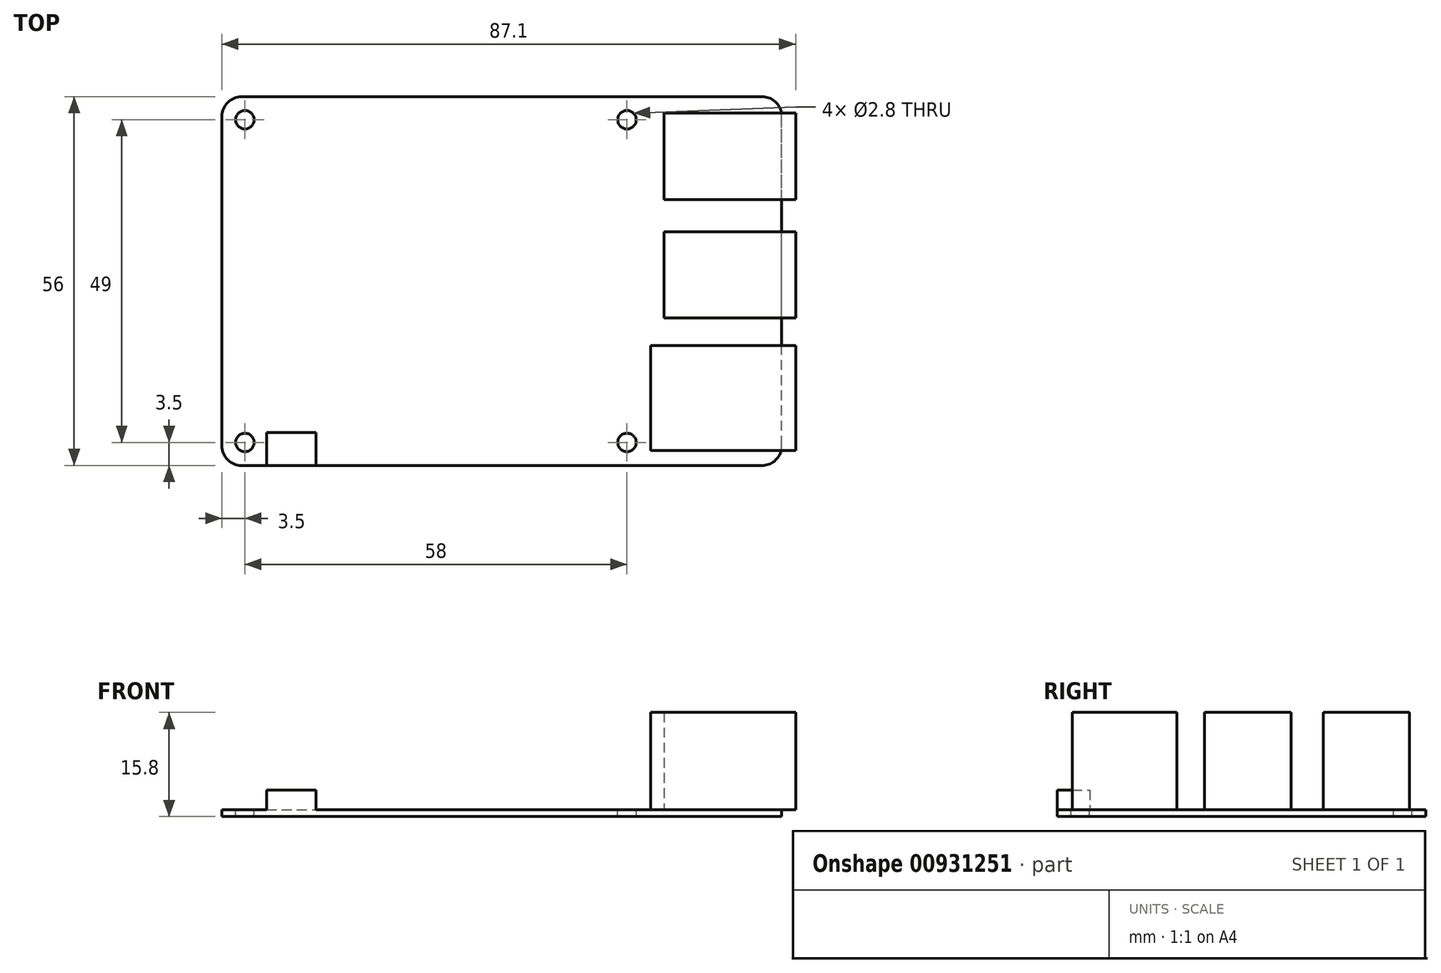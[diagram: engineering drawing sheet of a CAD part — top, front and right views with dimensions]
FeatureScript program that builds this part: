
annotation { "Feature Type Name" : "Feature", "Feature Type Description" : "" }
export const myFeature = defineFeature(function(context is Context, id is Id, definition is map)
    precondition{}
    {
        {
            var Q0;
            Q0=qCreatedBy(makeId("Top.planeOp"),FACE);
            var sketch = newSketch(context, id + "F0", { "sketchPlane" : qUnion([Q0])});
            skLineSegment(sketch, "E0.bottom", {"start": v(-42.5, -28) * mm, "end": v(42.5, -28) * mm});
            skLineSegment(sketch, "E0.top", {"start": v(-42.5, 28) * mm, "end": v(42.5, 28) * mm});
            skLineSegment(sketch, "E0.left", {"start": v(-42.5, -28) * mm, "end": v(-42.5, 28) * mm});
            skLineSegment(sketch, "E0.right", {"start": v(42.5, -28) * mm, "end": v(42.5, 28) * mm});
            skSolve(sketch);
        }
        {
            var Q0;
            Q0=qSketchRegion(id+"F0",true);
            extrude(context, id + "F1", {"entities" : qUnion([Q0]), "depth" : 1 * mm, "offsetDistance" : 25 * mm});
        }
        {
            var Q0;
            Q0=makeQuery(id+"F1.opExtrude","SWEPT_EDGE",EDGE,{"disambiguationData":[OSD([sQuery(id+"F0.wireOp",EDGE,"E0.bottom"),sQuery(id+"F0.wireOp",EDGE,"E0.right")])]});
            var Q1;
            Q1=makeQuery(id+"F1.opExtrude","SWEPT_EDGE",EDGE,{"disambiguationData":[OSD([sQuery(id+"F0.wireOp",EDGE,"E0.top"),sQuery(id+"F0.wireOp",EDGE,"E0.right")])]});
            var Q2;
            Q2=makeQuery(id+"F1.opExtrude","SWEPT_EDGE",EDGE,{"disambiguationData":[OSD([sQuery(id+"F0.wireOp",EDGE,"E0.top"),sQuery(id+"F0.wireOp",EDGE,"E0.left")])]});
            var Q3;
            Q3=makeQuery(id+"F1.opExtrude","SWEPT_EDGE",EDGE,{"disambiguationData":[OSD([sQuery(id+"F0.wireOp",EDGE,"E0.bottom"),sQuery(id+"F0.wireOp",EDGE,"E0.left")])]});
            fillet(context, id + "F2", {"entities" : qUnion([Q0, Q1, Q2, Q3]), "radius" : 3 * mm, "tangentPropagation" : true, "allowEdgeOverflow" : false});
        }
        {
            var Q0;
            Q0=makeQuery(id+"F1.opExtrude","CAP_FACE",FACE,{"disambiguationData":[OSD([sQuery(id+"F0.wireOp",EDGE,"E0.bottom"),sQuery(id+"F0.wireOp",EDGE,"E0.top"),sQuery(id+"F0.wireOp",EDGE,"E0.left"),sQuery(id+"F0.wireOp",EDGE,"E0.right")])],"isStart":false});
            var sketch = newSketch(context, id + "F3", { "sketchPlane" : qUnion([Q0])});
            skLineSegment(sketch, "E1.bottom", {"start": v(44.6, -25.7) * mm, "end": v(22.6, -25.7) * mm});
            skLineSegment(sketch, "E1.top", {"start": v(44.6, -9.8) * mm, "end": v(22.6, -9.8) * mm});
            skLineSegment(sketch, "E1.left", {"start": v(44.6, -25.7) * mm, "end": v(44.6, -9.8) * mm});
            skLineSegment(sketch, "E1.right", {"start": v(22.6, -25.7) * mm, "end": v(22.6, -9.8) * mm});
            skLineSegment(sketch, "E2.bottom", {"start": v(24.6, 7.5) * mm, "end": v(44.6, 7.5) * mm});
            skLineSegment(sketch, "E2.top", {"start": v(24.6, -5.6) * mm, "end": v(44.6, -5.6) * mm});
            skLineSegment(sketch, "E2.left", {"start": v(24.6, 7.5) * mm, "end": v(24.6, -5.6) * mm});
            skLineSegment(sketch, "E2.right", {"start": v(44.6, 7.5) * mm, "end": v(44.6, -5.6) * mm});
            skLineSegment(sketch, "E3.bottom", {"start": v(24.6, 25.5) * mm, "end": v(44.6, 25.5) * mm});
            skLineSegment(sketch, "E3.top", {"start": v(24.6, 12.4) * mm, "end": v(44.6, 12.4) * mm});
            skLineSegment(sketch, "E3.left", {"start": v(24.6, 25.5) * mm, "end": v(24.6, 12.4) * mm});
            skLineSegment(sketch, "E3.right", {"start": v(44.6, 25.5) * mm, "end": v(44.6, 12.4) * mm});
            skSolve(sketch);
        }
        {
            var Q0;
            Q0=qSketchRegion(id+"F3",true);
            extrude(context, id + "F4", {"entities" : qUnion([Q0]), "operationType" : NewBodyOperationType.ADD, "depth" : 14.8 * mm, "offsetDistance" : 25 * mm});
        }
        {
            var Q0;
            Q0=makeQuery(id+"F1.opExtrude","CAP_FACE",FACE,{"disambiguationData":[OSD([sQuery(id+"F0.wireOp",EDGE,"E0.bottom"),sQuery(id+"F0.wireOp",EDGE,"E0.top"),sQuery(id+"F0.wireOp",EDGE,"E0.left"),sQuery(id+"F0.wireOp",EDGE,"E0.right")])],"isStart":false});
            var sketch = newSketch(context, id + "F5", { "sketchPlane" : qUnion([Q0])});
            skPoint(sketch, "E4", {"position": v(-39, 24.5) * mm});
            skPoint(sketch, "E5", {"position": v(-39, -24.5) * mm});
            skPoint(sketch, "E6", {"position": v(19, -24.5) * mm});
            skPoint(sketch, "E7", {"position": v(19, 24.5) * mm});
            skSolve(sketch);
        }
        {
            var Q0;
            Q0=sQuery(id+"F5.wireOp",VERTEX,"E4");
            var Q1;
            Q1=sQuery(id+"F5.wireOp",VERTEX,"E7");
            var Q2;
            Q2=sQuery(id+"F5.wireOp",VERTEX,"E6");
            var Q3;
            Q3=sQuery(id+"F5.wireOp",VERTEX,"E5");
            var Q4;
            Q4=makeQuery(id+"F1.opExtrude","SWEPT_BODY",BODY,{"disambiguationData":[OSD([sQuery(id+"F0.wireOp",EDGE,"E0.bottom"),sQuery(id+"F0.wireOp",EDGE,"E0.top"),sQuery(id+"F0.wireOp",EDGE,"E0.left"),sQuery(id+"F0.wireOp",EDGE,"E0.right")])]});
            hole(context, id + "F6", {"style" : HoleStyle.SIMPLE, "endStyle" : HoleEndStyle.BLIND, "holeDiameter" : 2.8 * mm, "majorDiameter" : 5 * mm, "holeDepth" : 5 * mm, "isTappedThrough" : true, "tappedDepth" : 12 * mm, "tapClearance" : 3, "locations" : qUnion([Q0, Q1, Q2, Q3]), "scope" : qUnion([Q4])});
        }
        {
            var Q0;
            Q0=makeQuery(id+"F1.opExtrude","CAP_FACE",FACE,{"disambiguationData":[OSD([sQuery(id+"F0.wireOp",EDGE,"E0.bottom"),sQuery(id+"F0.wireOp",EDGE,"E0.top"),sQuery(id+"F0.wireOp",EDGE,"E0.left"),sQuery(id+"F0.wireOp",EDGE,"E0.right")])],"isStart":false});
            var sketch = newSketch(context, id + "F7", { "sketchPlane" : qUnion([Q0])});
            skLineSegment(sketch, "E8.bottom", {"start": v(-35.7, -28) * mm, "end": v(-28.2, -28) * mm});
            skLineSegment(sketch, "E8.top", {"start": v(-35.7, -23) * mm, "end": v(-28.2, -23) * mm});
            skLineSegment(sketch, "E8.left", {"start": v(-35.7, -28) * mm, "end": v(-35.7, -23) * mm});
            skLineSegment(sketch, "E8.right", {"start": v(-28.2, -28) * mm, "end": v(-28.2, -23) * mm});
            skSolve(sketch);
        }
        {
            var Q0;
            Q0=qSketchRegion(id+"F7",true);
            extrude(context, id + "F8", {"entities" : qUnion([Q0]), "operationType" : NewBodyOperationType.ADD, "depth" : 3 * mm, "offsetDistance" : 25 * mm});
        }
    });
